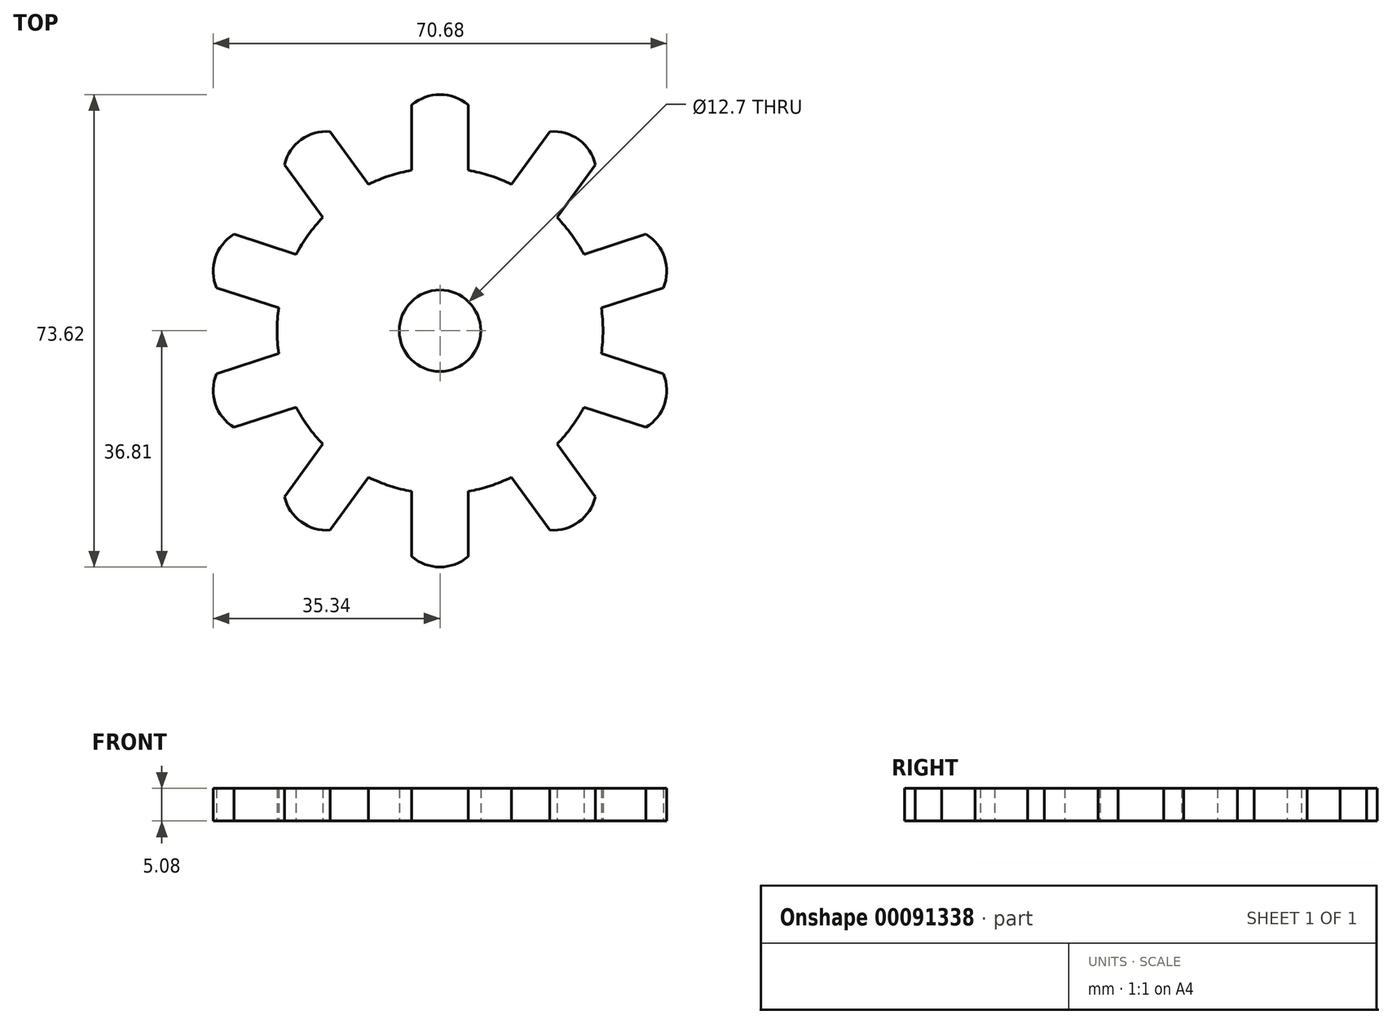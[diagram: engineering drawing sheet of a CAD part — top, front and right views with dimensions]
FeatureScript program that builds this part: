
annotation { "Feature Type Name" : "Feature", "Feature Type Description" : "" }
export const myFeature = defineFeature(function(context is Context, id is Id, definition is map)
    precondition{}
    {
        {
            var Q0;
            Q0=qCreatedBy(makeId("Top.planeOp"),FACE);
            var sketch = newSketch(context, id + "F0", { "sketchPlane" : qUnion([Q0])});
            skArc(sketch, "E0", {"start": v(-4.4, 25.02) * mm, "mid": v(-7.85, 24.16) * mm, "end": v(-11.15, 22.82) * mm});
            skLineSegment(sketch, "E1.left", {"start": v(4.4, 25.02) * mm, "end": v(4.4, 35.18) * mm});
            skLineSegment(sketch, "E1.right", {"start": v(-4.4, 25.02) * mm, "end": v(-4.4, 35.18) * mm});
            skArc(sketch, "E2", {"start": v(4.4, 35.18) * mm, "mid": v(0, 36.81) * mm, "end": v(-4.4, 35.18) * mm});
            skPoint(sketch, "E3.start.orphan", {"position": v(0, 35.18) * mm});
            skLineSegment(sketch, "E4.1.0", {"start": v(-11.15, 22.82) * mm, "end": v(-17.12, 31.04) * mm});
            skArc(sketch, "E4.1.1", {"start": v(-17.12, 31.04) * mm, "mid": v(-21.64, 29.78) * mm, "end": v(-24.23, 25.88) * mm});
            skLineSegment(sketch, "E4.1.2", {"start": v(-18.26, 17.66) * mm, "end": v(-24.23, 25.88) * mm});
            skLineSegment(sketch, "E4.2.0", {"start": v(-22.44, 11.9) * mm, "end": v(-32.1, 15.05) * mm});
            skArc(sketch, "E4.2.1", {"start": v(-32.1, 15.05) * mm, "mid": v(-35.01, 11.38) * mm, "end": v(-34.81, 6.7) * mm});
            skLineSegment(sketch, "E4.2.2", {"start": v(-25.15, 3.55) * mm, "end": v(-34.81, 6.7) * mm});
            skLineSegment(sketch, "E4.3.0", {"start": v(-25.15, -3.55) * mm, "end": v(-34.81, -6.7) * mm});
            skArc(sketch, "E4.3.1", {"start": v(-34.81, -6.7) * mm, "mid": v(-35.01, -11.38) * mm, "end": v(-32.1, -15.05) * mm});
            skLineSegment(sketch, "E4.3.2", {"start": v(-22.44, -11.9) * mm, "end": v(-32.1, -15.05) * mm});
            skLineSegment(sketch, "E4.4.0", {"start": v(-18.26, -17.66) * mm, "end": v(-24.23, -25.88) * mm});
            skArc(sketch, "E4.4.1", {"start": v(-24.23, -25.88) * mm, "mid": v(-21.64, -29.78) * mm, "end": v(-17.12, -31.04) * mm});
            skLineSegment(sketch, "E4.4.2", {"start": v(-11.15, -22.82) * mm, "end": v(-17.12, -31.04) * mm});
            skLineSegment(sketch, "E4.5.0", {"start": v(-4.4, -25.02) * mm, "end": v(-4.4, -35.18) * mm});
            skArc(sketch, "E4.5.1", {"start": v(-4.4, -35.18) * mm, "mid": v(0, -36.81) * mm, "end": v(4.4, -35.18) * mm});
            skLineSegment(sketch, "E4.5.2", {"start": v(4.4, -25.02) * mm, "end": v(4.4, -35.18) * mm});
            skLineSegment(sketch, "E4.6.0", {"start": v(11.15, -22.82) * mm, "end": v(17.12, -31.04) * mm});
            skArc(sketch, "E4.6.1", {"start": v(17.12, -31.04) * mm, "mid": v(21.64, -29.78) * mm, "end": v(24.23, -25.88) * mm});
            skLineSegment(sketch, "E4.6.2", {"start": v(18.26, -17.66) * mm, "end": v(24.23, -25.88) * mm});
            skLineSegment(sketch, "E4.7.0", {"start": v(22.44, -11.9) * mm, "end": v(32.1, -15.05) * mm});
            skArc(sketch, "E4.7.1", {"start": v(32.1, -15.05) * mm, "mid": v(35.01, -11.38) * mm, "end": v(34.81, -6.7) * mm});
            skLineSegment(sketch, "E4.7.2", {"start": v(25.15, -3.55) * mm, "end": v(34.81, -6.7) * mm});
            skLineSegment(sketch, "E4.8.0", {"start": v(25.15, 3.55) * mm, "end": v(34.81, 6.7) * mm});
            skArc(sketch, "E4.8.1", {"start": v(34.81, 6.7) * mm, "mid": v(35.01, 11.38) * mm, "end": v(32.1, 15.05) * mm});
            skLineSegment(sketch, "E4.8.2", {"start": v(22.44, 11.9) * mm, "end": v(32.1, 15.05) * mm});
            skLineSegment(sketch, "E4.9.0", {"start": v(18.26, 17.66) * mm, "end": v(24.23, 25.88) * mm});
            skArc(sketch, "E4.9.1", {"start": v(24.23, 25.88) * mm, "mid": v(21.64, 29.78) * mm, "end": v(17.12, 31.04) * mm});
            skLineSegment(sketch, "E4.9.2", {"start": v(11.15, 22.82) * mm, "end": v(17.12, 31.04) * mm});
            skArc(sketch, "E5.trimOffspring", {"start": v(-18.26, 17.66) * mm, "mid": v(-20.55, 14.93) * mm, "end": v(-22.44, 11.9) * mm});
            skArc(sketch, "E6.trimOffspring", {"start": v(-25.15, 3.55) * mm, "mid": v(-25.4, 0) * mm, "end": v(-25.15, -3.55) * mm});
            skArc(sketch, "E7.trimOffspring", {"start": v(-22.44, -11.9) * mm, "mid": v(-20.55, -14.93) * mm, "end": v(-18.26, -17.66) * mm});
            skArc(sketch, "E8.trimOffspring", {"start": v(-11.15, -22.82) * mm, "mid": v(-7.85, -24.16) * mm, "end": v(-4.4, -25.02) * mm});
            skArc(sketch, "E9.trimOffspring", {"start": v(4.4, -25.02) * mm, "mid": v(7.85, -24.16) * mm, "end": v(11.15, -22.82) * mm});
            skArc(sketch, "E10.trimOffspring", {"start": v(18.26, -17.66) * mm, "mid": v(20.55, -14.93) * mm, "end": v(22.44, -11.9) * mm});
            skArc(sketch, "E11.trimOffspring", {"start": v(25.15, -3.55) * mm, "mid": v(25.4, 0) * mm, "end": v(25.15, 3.55) * mm});
            skArc(sketch, "E12.trimOffspring", {"start": v(22.44, 11.9) * mm, "mid": v(20.55, 14.93) * mm, "end": v(18.26, 17.66) * mm});
            skArc(sketch, "E13.trimOffspring", {"start": v(11.15, 22.82) * mm, "mid": v(7.85, 24.16) * mm, "end": v(4.4, 25.02) * mm});
            skCircle(sketch, "E14", {"center": v(0, 0) * mm, "radius": 6.35 * mm});
            skSolve(sketch);
        }
        {
            var Q0;
            Q0=makeQuery(id+"F0.imprint","IMPRINT",FACE,{"disambiguationData":[TD([[makeQuery(id+"F0.imprint","IMPRINT",EDGE,{"derivedFrom":sQuery(id+"F0.wireOp",EDGE,"E0")}),1.0]])]});
            extrude(context, id + "F1", {"entities" : qUnion([Q0]), "depth" : 5.08 * mm});
        }
    });
